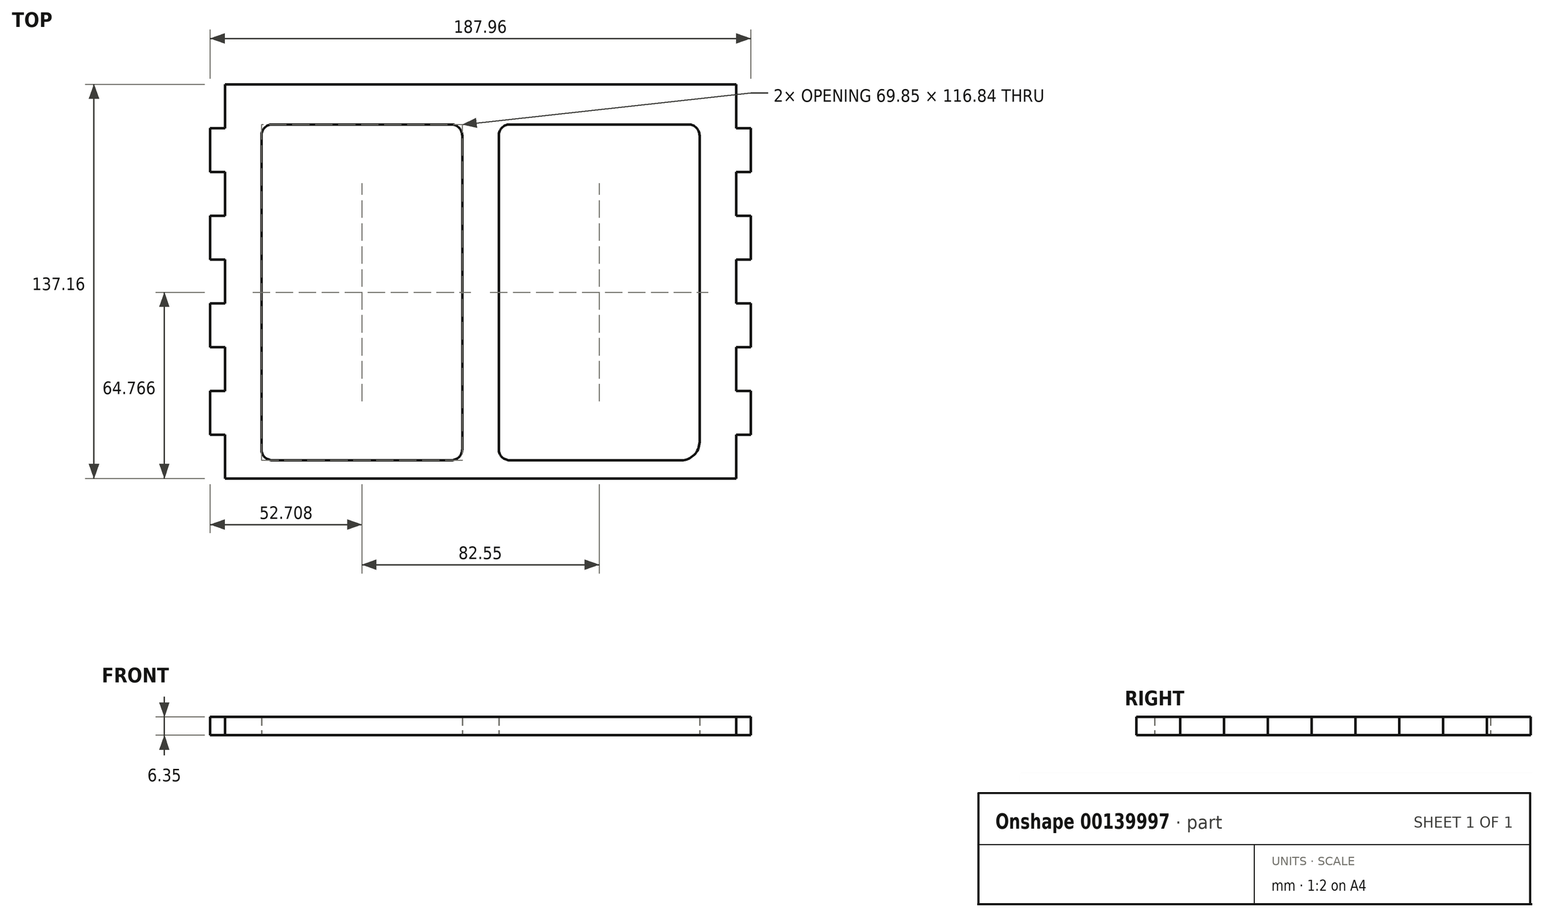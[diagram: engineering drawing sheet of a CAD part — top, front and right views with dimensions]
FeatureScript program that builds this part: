
annotation { "Feature Type Name" : "Feature", "Feature Type Description" : "" }
export const myFeature = defineFeature(function(context is Context, id is Id, definition is map)
    precondition{}
    {
        {
            var Q0;
            Q0=qCreatedBy(makeId("Top.planeOp"),FACE);
            var sketch = newSketch(context, id + "F0", { "sketchPlane" : qUnion([Q0])});
            skLineSegment(sketch, "E0", {"start": v(66.43, 75.28) * mm, "end": v(66.43, 60.04) * mm});
            skLineSegment(sketch, "E1", {"start": v(66.43, 60.04) * mm, "end": v(71.51, 60.04) * mm});
            skLineSegment(sketch, "E2", {"start": v(71.51, 60.04) * mm, "end": v(71.51, 44.8) * mm});
            skLineSegment(sketch, "E3", {"start": v(71.51, 44.8) * mm, "end": v(66.43, 44.8) * mm});
            skLineSegment(sketch, "E4", {"start": v(66.43, 44.8) * mm, "end": v(66.43, 29.56) * mm});
            skLineSegment(sketch, "E5", {"start": v(66.43, 29.56) * mm, "end": v(71.51, 29.56) * mm});
            skLineSegment(sketch, "E6", {"start": v(71.51, 29.56) * mm, "end": v(71.51, 14.32) * mm});
            skLineSegment(sketch, "E7", {"start": v(71.51, 14.32) * mm, "end": v(66.43, 14.32) * mm});
            skLineSegment(sketch, "E8", {"start": v(66.43, 14.32) * mm, "end": v(66.43, -0.92) * mm});
            skLineSegment(sketch, "E9", {"start": v(66.43, -0.92) * mm, "end": v(71.51, -0.92) * mm});
            skLineSegment(sketch, "E10", {"start": v(71.51, -0.92) * mm, "end": v(71.51, -16.16) * mm});
            skLineSegment(sketch, "E11", {"start": v(71.51, -16.16) * mm, "end": v(66.43, -16.16) * mm});
            skLineSegment(sketch, "E12", {"start": v(66.43, -16.16) * mm, "end": v(66.43, -31.4) * mm});
            skLineSegment(sketch, "E13", {"start": v(66.43, -31.4) * mm, "end": v(71.51, -31.4) * mm});
            skLineSegment(sketch, "E14", {"start": v(71.51, -31.4) * mm, "end": v(71.51, -46.64) * mm});
            skLineSegment(sketch, "E15", {"start": v(71.51, -46.64) * mm, "end": v(66.43, -46.64) * mm});
            skLineSegment(sketch, "E16", {"start": v(66.43, -46.64) * mm, "end": v(66.43, -61.88) * mm});
            skLineSegment(sketch, "E17", {"start": v(-111.37, 75.28) * mm, "end": v(-111.37, 60.04) * mm});
            skLineSegment(sketch, "E18", {"start": v(-111.37, 60.04) * mm, "end": v(-116.45, 60.04) * mm});
            skLineSegment(sketch, "E19", {"start": v(-116.45, 60.04) * mm, "end": v(-116.45, 44.8) * mm});
            skLineSegment(sketch, "E20", {"start": v(-116.45, 44.8) * mm, "end": v(-111.37, 44.8) * mm});
            skLineSegment(sketch, "E21", {"start": v(-111.37, 44.8) * mm, "end": v(-111.37, 29.56) * mm});
            skLineSegment(sketch, "E22", {"start": v(-111.37, 29.56) * mm, "end": v(-116.45, 29.56) * mm});
            skLineSegment(sketch, "E23", {"start": v(-116.45, 29.56) * mm, "end": v(-116.45, 14.32) * mm});
            skLineSegment(sketch, "E24", {"start": v(-116.45, 14.32) * mm, "end": v(-111.37, 14.32) * mm});
            skLineSegment(sketch, "E25", {"start": v(-111.37, 14.32) * mm, "end": v(-111.37, -0.92) * mm});
            skLineSegment(sketch, "E26", {"start": v(-111.37, -0.92) * mm, "end": v(-116.45, -0.92) * mm});
            skLineSegment(sketch, "E27", {"start": v(-116.45, -0.92) * mm, "end": v(-116.45, -16.16) * mm});
            skLineSegment(sketch, "E28", {"start": v(-116.45, -16.16) * mm, "end": v(-111.37, -16.16) * mm});
            skLineSegment(sketch, "E29", {"start": v(-111.37, -16.16) * mm, "end": v(-111.37, -31.4) * mm});
            skLineSegment(sketch, "E30", {"start": v(-111.37, -31.4) * mm, "end": v(-116.45, -31.4) * mm});
            skLineSegment(sketch, "E31", {"start": v(-116.45, -31.4) * mm, "end": v(-116.45, -46.64) * mm});
            skLineSegment(sketch, "E32", {"start": v(-116.45, -46.64) * mm, "end": v(-111.37, -46.64) * mm});
            skLineSegment(sketch, "E33", {"start": v(-111.37, -46.64) * mm, "end": v(-111.37, -61.88) * mm});
            skLineSegment(sketch, "E34", {"start": v(-107.64, 0) * mm, "end": v(50.36, 0) * mm, "construction": true});
            skLineSegment(sketch, "E35", {"start": v(-111.37, 75.28) * mm, "end": v(66.43, 75.28) * mm});
            skLineSegment(sketch, "E36", {"start": v(-111.37, -61.88) * mm, "end": v(66.43, -61.88) * mm});
            skLineSegment(sketch, "E37.bottom", {"start": v(-94.86, 61.3) * mm, "end": v(-32.63, 61.3) * mm});
            skLineSegment(sketch, "E37.top", {"start": v(-94.86, -55.53) * mm, "end": v(-32.63, -55.53) * mm});
            skLineSegment(sketch, "E37.left", {"start": v(-98.67, 57.5) * mm, "end": v(-98.67, -51.72) * mm});
            skLineSegment(sketch, "E37.right", {"start": v(-28.82, 57.5) * mm, "end": v(-28.82, -51.72) * mm});
            skPoint(sketch, "E38.visualSharp", {"position": v(-98.67, 61.3) * mm});
            skArc(sketch, "E38.filletArc", {"start": v(-94.86, 61.3) * mm, "mid": v(-97.55, 60.19) * mm, "end": v(-98.67, 57.5) * mm});
            skPoint(sketch, "E39.visualSharp", {"position": v(-28.82, 61.3) * mm});
            skArc(sketch, "E39.filletArc", {"start": v(-28.82, 57.5) * mm, "mid": v(-29.93, 60.19) * mm, "end": v(-32.63, 61.3) * mm});
            skPoint(sketch, "E40.visualSharp", {"position": v(-28.82, -55.53) * mm});
            skArc(sketch, "E40.filletArc", {"start": v(-32.63, -55.53) * mm, "mid": v(-29.93, -54.42) * mm, "end": v(-28.82, -51.72) * mm});
            skPoint(sketch, "E41.visualSharp", {"position": v(-98.67, -55.53) * mm});
            skArc(sketch, "E41.filletArc", {"start": v(-98.67, -51.72) * mm, "mid": v(-97.55, -54.42) * mm, "end": v(-94.86, -55.53) * mm});
            skPoint(sketch, "E42.oppositeSnap0", {"position": v(-63.74, -55.53) * mm});
            skLineSegment(sketch, "E42.bottom", {"start": v(-12.3, 61.3) * mm, "end": v(49.92, 61.3) * mm});
            skLineSegment(sketch, "E42.top", {"start": v(-12.3, -55.53) * mm, "end": v(47.38, -55.53) * mm});
            skLineSegment(sketch, "E42.left", {"start": v(-16.12, 57.5) * mm, "end": v(-16.12, -51.72) * mm});
            skLineSegment(sketch, "E42.right", {"start": v(53.73, 57.5) * mm, "end": v(53.73, -49.18) * mm});
            skPoint(sketch, "E43.visualSharp", {"position": v(-16.12, 61.3) * mm});
            skArc(sketch, "E43.filletArc", {"start": v(-12.3, 61.3) * mm, "mid": v(-15, 60.19) * mm, "end": v(-16.12, 57.5) * mm});
            skPoint(sketch, "E44.visualSharp", {"position": v(53.73, 61.3) * mm});
            skArc(sketch, "E44.filletArc", {"start": v(53.73, 57.5) * mm, "mid": v(52.62, 60.19) * mm, "end": v(49.92, 61.3) * mm});
            skPoint(sketch, "E45.visualSharp", {"position": v(53.73, -55.53) * mm});
            skArc(sketch, "E45.filletArc", {"start": v(47.38, -55.53) * mm, "mid": v(51.87, -53.67) * mm, "end": v(53.73, -49.18) * mm});
            skPoint(sketch, "E46.visualSharp", {"position": v(-16.12, -55.53) * mm});
            skArc(sketch, "E46.filletArc", {"start": v(-16.12, -51.72) * mm, "mid": v(-15, -54.42) * mm, "end": v(-12.3, -55.53) * mm});
            skSolve(sketch);
        }
        {
            var Q0;
            Q0=makeQuery(id+"F0.imprint","IMPRINT",FACE,{"disambiguationData":[TD([[makeQuery(id+"F0.imprint","IMPRINT",EDGE,{"derivedFrom":sQuery(id+"F0.wireOp",EDGE,"E0")}),-1.0]])]});
            extrude(context, id + "F1", {"entities" : qUnion([Q0]), "depth" : 6.35 * mm});
        }
    });
